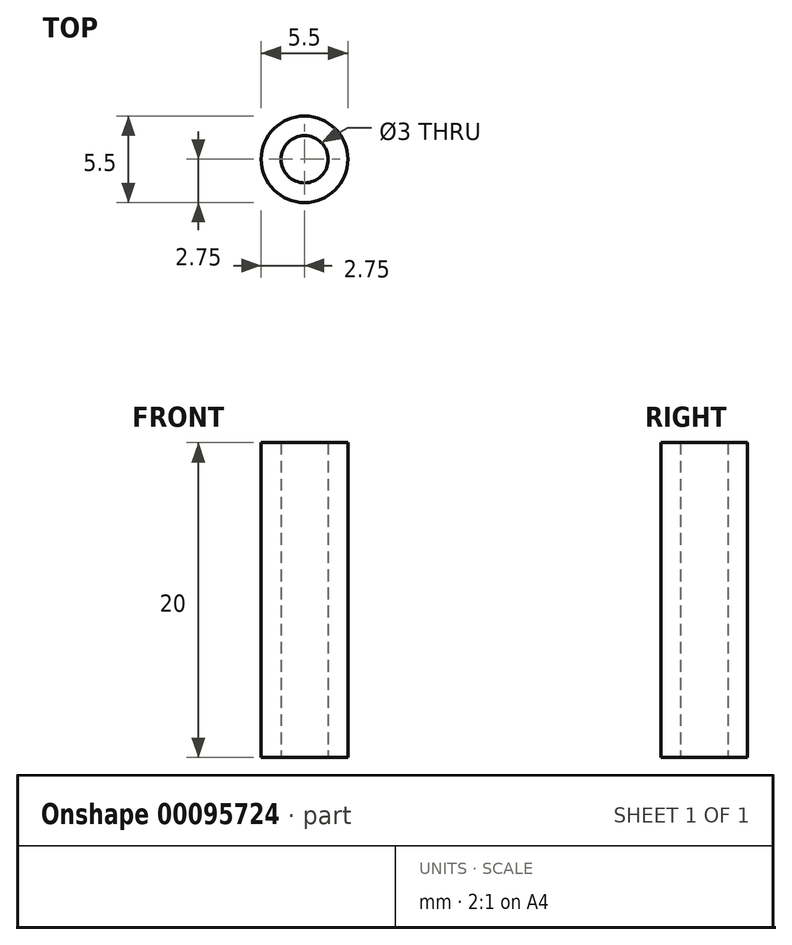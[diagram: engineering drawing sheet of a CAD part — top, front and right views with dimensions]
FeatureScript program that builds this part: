
annotation { "Feature Type Name" : "Feature", "Feature Type Description" : "" }
export const myFeature = defineFeature(function(context is Context, id is Id, definition is map)
    precondition{}
    {
        {
            var Q0;
            Q0=qCreatedBy(makeId("Top.planeOp"),FACE);
            var sketch = newSketch(context, id + "F0", { "sketchPlane" : qUnion([Q0])});
            skCircle(sketch, "E0", {"center": v(0, 0) * mm, "radius": 1.5 * mm});
            skCircle(sketch, "E1", {"center": v(0, 0) * mm, "radius": 2.75 * mm});
            skSolve(sketch);
        }
        {
            var Q0;
            Q0=qSketchRegion(id+"F0",true);
            extrude(context, id + "F1", {"entities" : qUnion([Q0]), "depth" : 20 * mm});
        }
    });
